# Revit family: Faucet-Kitchen-Delta-Essa_Single_Handle_Pull_Down_9913-dst
name_source: partatom
category: Plumbing Fixtures
revit_build: Autodesk Revit MEP 2012 (Build: 20110916_2132(x64)
units: mm (PartAtom-declared; Revit-internal decimal feet)

## types (4) — shared parameters
Date Modified = October 6, 2015
Default Elevation = 48 "
Equipment Abbreviation = BF
Family Version = 1.0
Manufacturer = Delta Faucet Company
Model Disclaimer = Contact Delta Faucet Company for More Information
Product Documentation Link = http://www.deltafaucet.com
Product Page URL = http://www.deltafaucet.com
URL = http://www.deltafaucet.com

## per-type parameters (varying)
| type | Description | Finish Material | Model | z Type |
| Arctic Stainless | Essa Kitchen, Bar Faucet, Arctic Steel | Stainless Steel - Delta - Brushed | 9913-AR-DST | 1 |
| Chrome | Essa Kitchen, Bar Faucet, Polished Chrome | Chrome - Delta - Polished | 9913-DST | 3 |
| Venetian Bronze | Essa Kitchen, Bar Faucet, Venetian Bronze | Bronze - Delta - Venetian | 9913-RB-DST | 2 |
| Matte Black | Essa Kitchen, Bar Faucet, Matte Black | Stainless Steel - Delta - Matte Black | 9913-BL-DST | 4 |

## geometry (parser evidence)
native form markers: Sweep x2
no freeform markers — native parametric forms only
